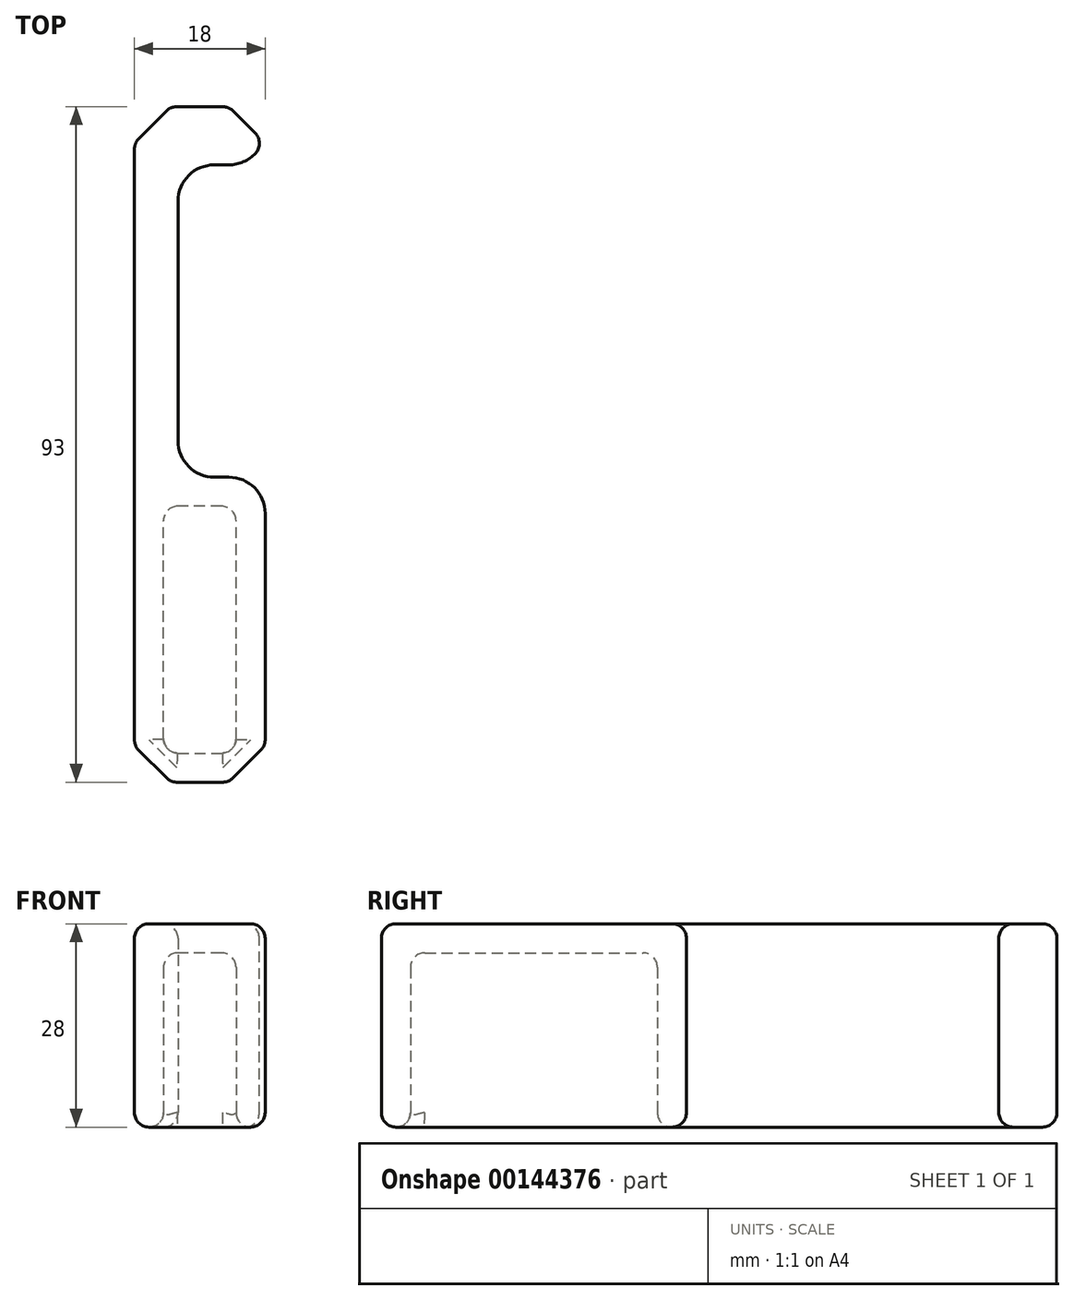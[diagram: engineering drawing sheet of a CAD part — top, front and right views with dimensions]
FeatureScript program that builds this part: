
annotation { "Feature Type Name" : "Feature", "Feature Type Description" : "" }
export const myFeature = defineFeature(function(context is Context, id is Id, definition is map)
    precondition{}
    {
        {
            var Q0;
            Q0=qCreatedBy(makeId("Top.planeOp"),FACE);
            var sketch = newSketch(context, id + "F0", { "sketchPlane" : qUnion([Q0])});
            skLineSegment(sketch, "E0.bottom", {"start": v(0, 0) * mm, "end": v(18, 0) * mm});
            skLineSegment(sketch, "E0.top", {"start": v(0, 93) * mm, "end": v(18, 93) * mm});
            skLineSegment(sketch, "E0.left", {"start": v(0, 0) * mm, "end": v(0, 93) * mm});
            skLineSegment(sketch, "E0.right", {"start": v(18, 0) * mm, "end": v(18, 42) * mm});
            skLineSegment(sketch, "E1", {"start": v(18, 42) * mm, "end": v(6, 42) * mm});
            skLineSegment(sketch, "E2", {"start": v(18, 85) * mm, "end": v(6, 85) * mm});
            skLineSegment(sketch, "E3", {"start": v(6, 85) * mm, "end": v(6, 42) * mm});
            skLineSegment(sketch, "E4.trimOffspring", {"start": v(18, 85) * mm, "end": v(18, 93) * mm});
            skSolve(sketch);
        }
        {
            var Q0;
            Q0 = qSketchRegion(id + "F0", true);
            extrude(context, id + "F1", {"entities" : qUnion([Q0]), "depth" : 28 * mm});
        }
        {
            var Q0;
            Q0=makeQuery(id+"F1.opExtrude","CAP_FACE",FACE,{"disambiguationData":[OSD([sQuery(id+"F0.wireOp",EDGE,"E0.bottom"),sQuery(id+"F0.wireOp",EDGE,"E0.top"),sQuery(id+"F0.wireOp",EDGE,"E0.left"),sQuery(id+"F0.wireOp",EDGE,"E0.right"),sQuery(id+"F0.wireOp",EDGE,"E1"),sQuery(id+"F0.wireOp",EDGE,"E2"),sQuery(id+"F0.wireOp",EDGE,"E3"),sQuery(id+"F0.wireOp",EDGE,"E4.trimOffspring")])],"isStart":true});
            shell(context, id + "F2", {"entities" : qUnion([Q0]), "thickness" : 4 * mm});
        }
        {
            var Q0;
            Q0=makeQuery(id+"F1.opExtrude","SWEPT_EDGE",EDGE,{"disambiguationData":[OSD([sQuery(id+"F0.wireOp",EDGE,"E2"),sQuery(id+"F0.wireOp",EDGE,"E3")])]});
            var Q1;
            Q1=makeQuery(id+"F1.opExtrude","SWEPT_EDGE",EDGE,{"disambiguationData":[OSD([sQuery(id+"F0.wireOp",EDGE,"E1"),sQuery(id+"F0.wireOp",EDGE,"E3")])]});
            var Q2;
            Q2=makeQuery(id+"F1.opExtrude","SWEPT_EDGE",EDGE,{"disambiguationData":[OSD([sQuery(id+"F0.wireOp",EDGE,"E0.right"),sQuery(id+"F0.wireOp",EDGE,"E1")])]});
            var Q3;
            Q3=makeQuery(id+"F1.opExtrude","SWEPT_EDGE",EDGE,{"disambiguationData":[OSD([sQuery(id+"F0.wireOp",EDGE,"E2"),sQuery(id+"F0.wireOp",EDGE,"E4.trimOffspring")])]});
            fillet(context, id + "F3", {"entities" : qUnion([Q0, Q1, Q2, Q3]), "radius" : 5 * mm, "tangentPropagation" : true, "allowEdgeOverflow" : false});
        }
        {
            var Q0;
            Q0=makeQuery(id+"F1.opExtrude","SWEPT_EDGE",EDGE,{"disambiguationData":[OSD([sQuery(id+"F0.wireOp",EDGE,"E0.bottom"),sQuery(id+"F0.wireOp",EDGE,"E0.left")])]});
            var Q1;
            Q1=makeQuery(id+"F1.opExtrude","SWEPT_EDGE",EDGE,{"disambiguationData":[OSD([sQuery(id+"F0.wireOp",EDGE,"E0.bottom"),sQuery(id+"F0.wireOp",EDGE,"E0.right")])]});
            var Q2;
            Q2=makeQuery(id+"F1.opExtrude","SWEPT_EDGE",EDGE,{"disambiguationData":[OSD([sQuery(id+"F0.wireOp",EDGE,"E0.top"),sQuery(id+"F0.wireOp",EDGE,"E4.trimOffspring")])]});
            var Q3;
            Q3=makeQuery(id+"F1.opExtrude","SWEPT_EDGE",EDGE,{"disambiguationData":[OSD([sQuery(id+"F0.wireOp",EDGE,"E0.top"),sQuery(id+"F0.wireOp",EDGE,"E0.left")])]});
            chamfer(context, id + "F4", {"entities" : qUnion([Q0, Q1, Q2, Q3]), "width" : 5 * mm, "tangentPropagation" : true});
        }
        {
            var Q0;
            Q0=makeQuery(id+"F1.opExtrude","CAP_FACE",FACE,{"disambiguationData":[OSD([sQuery(id+"F0.wireOp",EDGE,"E0.bottom"),sQuery(id+"F0.wireOp",EDGE,"E0.top"),sQuery(id+"F0.wireOp",EDGE,"E0.left"),sQuery(id+"F0.wireOp",EDGE,"E0.right"),sQuery(id+"F0.wireOp",EDGE,"E1"),sQuery(id+"F0.wireOp",EDGE,"E2"),sQuery(id+"F0.wireOp",EDGE,"E3"),sQuery(id+"F0.wireOp",EDGE,"E4.trimOffspring")])],"isStart":false});
            var Q1;
            Q1=makeQuery(id+"F1.opExtrude","SWEPT_FACE",FACE,{"disambiguationData":[OSD([sQuery(id+"F0.wireOp",EDGE,"E0.left")])]});
            var Q2;
            Q2=makeQuery(id+"F4.opChamfer","BLEND_FACE",FACE,{"disambiguationData":[OSD([sQuery(id+"F0.wireOp",EDGE,"E0.top"),sQuery(id+"F0.wireOp",EDGE,"E0.left")])]});
            var Q3;
            Q3=makeQuery(id+"F4.opChamfer","BLEND_FACE",FACE,{"disambiguationData":[OSD([sQuery(id+"F0.wireOp",EDGE,"E0.top"),sQuery(id+"F0.wireOp",EDGE,"E4.trimOffspring")])]});
            var Q4;
            Q4=makeQuery(id+"F1.opExtrude","SWEPT_FACE",FACE,{"disambiguationData":[OSD([sQuery(id+"F0.wireOp",EDGE,"E0.top")])]});
            var Q5;
            Q5=makeQuery(id+"F1.opExtrude","SWEPT_FACE",FACE,{"disambiguationData":[OSD([sQuery(id+"F0.wireOp",EDGE,"E0.right")])]});
            var Q6;
            Q6=makeQuery(id+"F4.opChamfer","BLEND_FACE",FACE,{"disambiguationData":[OSD([sQuery(id+"F0.wireOp",EDGE,"E0.bottom"),sQuery(id+"F0.wireOp",EDGE,"E0.right")])]});
            var Q7;
            Q7=makeQuery(id+"F1.opExtrude","SWEPT_FACE",FACE,{"disambiguationData":[OSD([sQuery(id+"F0.wireOp",EDGE,"E0.bottom")])]});
            var Q8;
            Q8=makeQuery(id+"F4.opChamfer","BLEND_FACE",FACE,{"disambiguationData":[OSD([sQuery(id+"F0.wireOp",EDGE,"E0.bottom"),sQuery(id+"F0.wireOp",EDGE,"E0.left")])]});
            var Q9;
            Q9=makeQuery(id+"F2.opShell","OFFSET_FACE",FACE,{"disambiguationData":[OSD([sQuery(id+"F0.wireOp",EDGE,"E0.bottom"),sQuery(id+"F0.wireOp",EDGE,"E0.top"),sQuery(id+"F0.wireOp",EDGE,"E0.left"),sQuery(id+"F0.wireOp",EDGE,"E0.right"),sQuery(id+"F0.wireOp",EDGE,"E1"),sQuery(id+"F0.wireOp",EDGE,"E2"),sQuery(id+"F0.wireOp",EDGE,"E3"),sQuery(id+"F0.wireOp",EDGE,"E4.trimOffspring")])]});
            var Q10;
            Q10=makeQuery(id+"F2.opShell","TWEAK_EDGE",EDGE,{"derivedFrom":[makeQuery(id+"F1.opExtrude","SWEPT_FACE",FACE,{"disambiguationData":[OSD([sQuery(id+"F0.wireOp",EDGE,"E0.left")])]}),makeQuery(id+"F1.opExtrude","SWEPT_FACE",FACE,{"disambiguationData":[OSD([sQuery(id+"F0.wireOp",EDGE,"E1")])]})]});
            var Q11;
            Q11=makeQuery(id+"F2.opShell","OFFSET_EDGE",EDGE,{"disambiguationData":[OSD([sQuery(id+"F0.wireOp",EDGE,"E0.right"),sQuery(id+"F0.wireOp",EDGE,"E1")])]});
            var Q12;
            Q12=makeQuery(id+"F2.opShell","OFFSET_EDGE",EDGE,{"disambiguationData":[OSD([sQuery(id+"F0.wireOp",EDGE,"E0.bottom"),sQuery(id+"F0.wireOp",EDGE,"E0.right")])]});
            var Q13;
            Q13=makeQuery(id+"F2.opShell","OFFSET_EDGE",EDGE,{"disambiguationData":[OSD([sQuery(id+"F0.wireOp",EDGE,"E0.bottom"),sQuery(id+"F0.wireOp",EDGE,"E0.left")])]});
            fillet(context, id + "F5", {"entities" : qUnion([Q0, Q1, Q2, Q3, Q4, Q5, Q6, Q7, Q8, Q9, Q10, Q11, Q12, Q13]), "radius" : 2 * mm, "tangentPropagation" : true, "allowEdgeOverflow" : false});
        }
        {
            var Q0;
            Q0=makeQuery(id+"F1.opExtrude","CAP_FACE",FACE,{"disambiguationData":[OSD([sQuery(id+"F0.wireOp",EDGE,"E0.bottom"),sQuery(id+"F0.wireOp",EDGE,"E0.top"),sQuery(id+"F0.wireOp",EDGE,"E0.left"),sQuery(id+"F0.wireOp",EDGE,"E0.right"),sQuery(id+"F0.wireOp",EDGE,"E1"),sQuery(id+"F0.wireOp",EDGE,"E2"),sQuery(id+"F0.wireOp",EDGE,"E3"),sQuery(id+"F0.wireOp",EDGE,"E4.trimOffspring")])],"isStart":true});
            fillet(context, id + "F6", {"entities" : qUnion([Q0]), "radius" : 2 * mm, "tangentPropagation" : true, "allowEdgeOverflow" : false});
        }
    });
